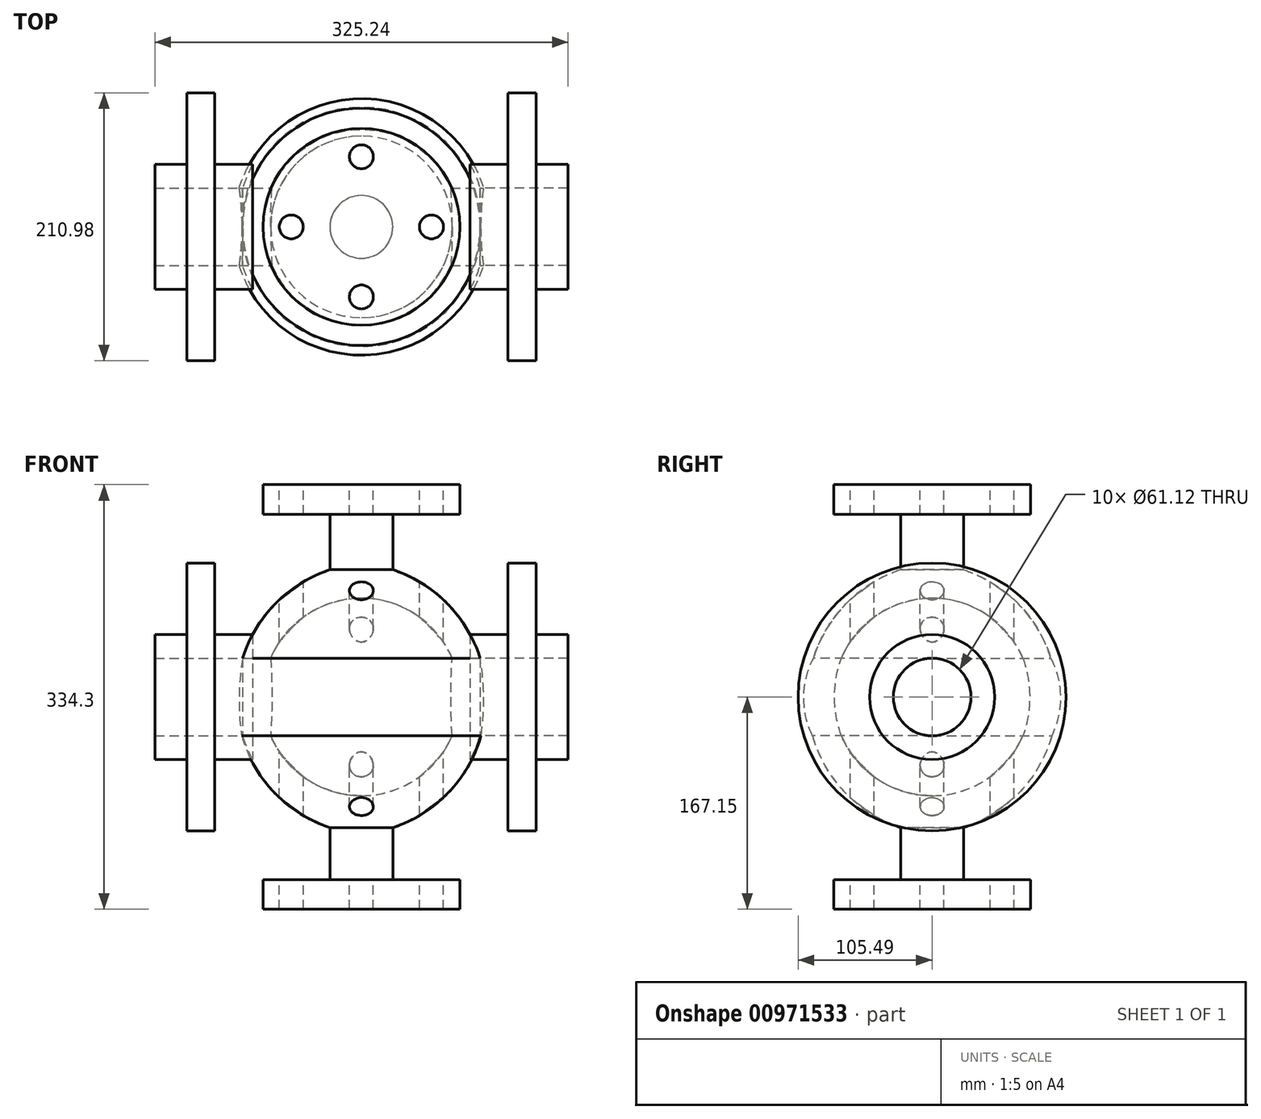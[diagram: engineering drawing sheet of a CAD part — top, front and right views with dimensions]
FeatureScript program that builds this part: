
annotation { "Feature Type Name" : "Feature", "Feature Type Description" : "" }
export const myFeature = defineFeature(function(context is Context, id is Id, definition is map)
    precondition{}
    {
        {
            var Q0;
            Q0=qCreatedBy(makeId("Front.planeOp"),FACE);
            var sketch = newSketch(context, id + "F0", { "sketchPlane" : qUnion([Q0])});
            skLineSegment(sketch, "E0", {"start": v(0, 77.72) * mm, "end": v(0, -77.72) * mm, "construction": true});
            skArc(sketch, "E1", {"start": v(0, -77.72) * mm, "mid": v(42.8, -64.87) * mm, "end": v(71.46, -30.56) * mm});
            skArc(sketch, "E2", {"start": v(23.44, -103.24) * mm, "mid": v(68, -75.84) * mm, "end": v(94.21, -30.56) * mm});
            skLineSegment(sketch, "E3", {"start": v(0, 77.72) * mm, "end": v(0, 167.15) * mm});
            skLineSegment(sketch, "E4", {"start": v(0, 167.15) * mm, "end": v(77.5, 167.15) * mm});
            skLineSegment(sketch, "E5", {"start": v(77.5, 167.15) * mm, "end": v(77.5, 143.7) * mm});
            skLineSegment(sketch, "E6", {"start": v(77.5, 143.7) * mm, "end": v(24.72, 143.7) * mm});
            skLineSegment(sketch, "E7", {"start": v(24.72, 143.7) * mm, "end": v(24.72, 100.18) * mm});
            skLineSegment(sketch, "E8", {"start": v(93.42, 30.56) * mm, "end": v(162.62, 30.56) * mm});
            skLineSegment(sketch, "E9", {"start": v(162.62, 30.56) * mm, "end": v(162.62, 49.22) * mm});
            skLineSegment(sketch, "E10", {"start": v(162.62, 49.22) * mm, "end": v(85.57, 49.22) * mm});
            skLineSegment(sketch, "E11", {"start": v(85.57, 49.22) * mm, "end": v(137.5, 49.22) * mm});
            skLineSegment(sketch, "E12", {"start": v(137.5, 49.22) * mm, "end": v(137.5, 105.49) * mm});
            skLineSegment(sketch, "E13", {"start": v(137.5, 105.49) * mm, "end": v(115.36, 105.49) * mm});
            skLineSegment(sketch, "E14", {"start": v(115.36, 105.49) * mm, "end": v(115.36, 49.22) * mm});
            skLineSegment(sketch, "E15", {"start": v(0, 0) * mm, "end": v(201.59, 0) * mm, "construction": true});
            skLineSegment(sketch, "E16.MirrorCS", {"start": v(94.21, -30.56) * mm, "end": v(162.62, -30.56) * mm});
            skLineSegment(sketch, "E17.MirrorCS", {"start": v(162.62, -30.56) * mm, "end": v(162.62, -49.22) * mm});
            skLineSegment(sketch, "E18.MirrorCS", {"start": v(162.62, -49.22) * mm, "end": v(85.57, -49.22) * mm});
            skLineSegment(sketch, "E19.MirrorCS", {"start": v(137.5, -49.22) * mm, "end": v(137.5, -105.49) * mm});
            skLineSegment(sketch, "E20.MirrorCS", {"start": v(115.36, -105.49) * mm, "end": v(115.36, -49.22) * mm});
            skLineSegment(sketch, "E21.MirrorCS", {"start": v(137.5, -105.49) * mm, "end": v(115.36, -105.49) * mm});
            skLineSegment(sketch, "E22.MirrorCS", {"start": v(24.72, -143.7) * mm, "end": v(24.72, -100.18) * mm});
            skLineSegment(sketch, "E23.MirrorCS", {"start": v(77.5, -143.7) * mm, "end": v(24.72, -143.7) * mm});
            skLineSegment(sketch, "E24.MirrorCS", {"start": v(77.5, -167.15) * mm, "end": v(77.5, -143.7) * mm});
            skLineSegment(sketch, "E25.MirrorCS", {"start": v(0, -167.15) * mm, "end": v(77.5, -167.15) * mm});
            skLineSegment(sketch, "E26.MirrorCS", {"start": v(0, -77.72) * mm, "end": v(0, -167.15) * mm});
            skPoint(sketch, "E27.orphan", {"position": v(71.46, -30.56) * mm});
            skPoint(sketch, "E28.orphan", {"position": v(71.46, 30.56) * mm});
            skArc(sketch, "E29.trimOffspring", {"start": v(93.42, 30.56) * mm, "mid": v(67.5, 73.7) * mm, "end": v(24.72, 100.18) * mm});
            skArc(sketch, "E30.trimOffspring", {"start": v(71.46, 30.56) * mm, "mid": v(42.8, 64.87) * mm, "end": v(0, 77.72) * mm});
            skArc(sketch, "E31", {"start": v(71.46, -30.56) * mm, "mid": v(76.77, 0) * mm, "end": v(71.46, 30.56) * mm});
            skArc(sketch, "E32", {"start": v(94.21, -30.56) * mm, "mid": v(100.97, 0.1) * mm, "end": v(93.42, 30.56) * mm});
            skSolve(sketch);
        }
        {
            var Q0;
            Q0=makeQuery(id+"F0.imprint","IMPRINT",FACE,{"disambiguationData":[TD([[makeQuery(id+"F0.imprint","IMPRINT",EDGE,{"derivedFrom":sQuery(id+"F0.wireOp",EDGE,"E1")}),-1.0]])]});
            var Q1;
            Q1=sQuery(id+"F0.wireOp",EDGE,"E0");
            revolve(context, id + "F1", {"surfaceOperationType" : NewSurfaceOperationType.NEW, "entities" : qUnion([Q0]), "axis" : qUnion([Q1]), "revolveType" : RevolveType.FULL});
        }
        {
            var Q0;
            {var subQ5=sQuery(id+"F0.wireOp",EDGE,"E8");Q0=makeQuery(id+"F0.imprint","IMPRINT",FACE,{"disambiguationData":[TD([[makeQuery(id+"F0.imprint","IMPRINT",EDGE,{"derivedFrom":subQ5}),1.0]])]});}
            var Q1;
            {var subQ0=sQuery(id+"F0.wireOp",EDGE,"E12");Q1=makeQuery(id+"F0.imprint","IMPRINT",FACE,{"disambiguationData":[TD([[makeQuery(id+"F0.imprint","IMPRINT",EDGE,{"derivedFrom":subQ0}),1.0]])]});}
            var Q2;
            Q2=sQuery(id+"F0.wireOp",EDGE,"E15");
            revolve(context, id + "F2", {"surfaceOperationType" : NewSurfaceOperationType.NEW, "entities" : qUnion([Q0, Q1]), "axis" : qUnion([Q2]), "revolveType" : RevolveType.FULL});
        }
        {
            var Q0;
            Q0=makeQuery(id+"F2.opRevolve","SWEPT_BODY",BODY,{"disambiguationData":[OSD([sQuery(id+"F0.wireOp",EDGE,"E8"),sQuery(id+"F0.wireOp",EDGE,"E9"),sQuery(id+"F0.wireOp",EDGE,"E10"),sQuery(id+"F0.wireOp",EDGE,"E11"),sQuery(id+"F0.wireOp",EDGE,"E12"),sQuery(id+"F0.wireOp",EDGE,"E13"),sQuery(id+"F0.wireOp",EDGE,"E14"),sQuery(id+"F0.wireOp",EDGE,"E29.trimOffspring")])]});
            var Q1;
            Q1=qCreatedBy(makeId("Right.planeOp"),FACE);
            mirror(context, id + "F3", {"entities" : qUnion([Q0]), "mirrorPlane" : qUnion([Q1])});
        }
        {
            var Q0;
            Q0=makeQuery(id+"F1.opRevolve","SWEPT_FACE",FACE,{"disambiguationData":[OSD([sQuery(id+"F0.wireOp",EDGE,"E4")])]});
            var sketch = newSketch(context, id + "F4", { "sketchPlane" : qUnion([Q0])});
            skCircle(sketch, "E33", {"center": v(0, 0) * mm, "radius": 19.05 * mm});
            skCircle(sketch, "E34", {"center": v(0, 55.18) * mm, "radius": 9.4 * mm});
            skSolve(sketch);
        }
        {
            var Q0;
            Q0=makeQuery(id+"F4.imprint","IMPRINT",FACE,{"disambiguationData":[TD([[makeQuery(id+"F4.imprint","IMPRINT",EDGE,{"derivedFrom":sQuery(id+"F4.wireOp",EDGE,"E33")}),-1.0]])]});
            var Q1;
            Q1=makeQuery(id+"F4.imprint","IMPRINT",FACE,{"disambiguationData":[TD([[makeQuery(id+"F4.imprint","IMPRINT",EDGE,{"derivedFrom":sQuery(id+"F4.wireOp",EDGE,"E34")}),1.0]])]});
            extrude(context, id + "F5", {"entities" : qUnion([Q0, Q1]), "operationType" : NewBodyOperationType.REMOVE, "endBound" : BoundingType.THROUGH_ALL, "oppositeDirection" : true, "depth" : 25.4 * mm, "offsetDistance" : 25.4 * mm});
        }
        {
            var Q0;
            Q0=makeQuery(id+"F1.opRevolve","SWEPT_BODY",BODY,{"disambiguationData":[OSD([sQuery(id+"F0.wireOp",EDGE,"E1"),sQuery(id+"F0.wireOp",EDGE,"E2"),sQuery(id+"F0.wireOp",EDGE,"E3"),sQuery(id+"F0.wireOp",EDGE,"E4"),sQuery(id+"F0.wireOp",EDGE,"E5"),sQuery(id+"F0.wireOp",EDGE,"E6"),sQuery(id+"F0.wireOp",EDGE,"E7"),sQuery(id+"F0.wireOp",EDGE,"E22.MirrorCS"),sQuery(id+"F0.wireOp",EDGE,"E23.MirrorCS"),sQuery(id+"F0.wireOp",EDGE,"E24.MirrorCS"),sQuery(id+"F0.wireOp",EDGE,"E25.MirrorCS"),sQuery(id+"F0.wireOp",EDGE,"E26.MirrorCS"),sQuery(id+"F0.wireOp",EDGE,"E29.trimOffspring"),sQuery(id+"F0.wireOp",EDGE,"E30.trimOffspring"),sQuery(id+"F0.wireOp",EDGE,"E31"),sQuery(id+"F0.wireOp",EDGE,"E32")])]});
            var Q1;
            Q1=sQuery(id+"F0.wireOp",EDGE,"E0");
            circularPattern(context, id + "F6", {"entities" : qUnion([Q0]), "axis" : qUnion([Q1]), "angle" : 360 * degree, "instanceCount" : 4, "equalSpace" : true});
        }
        {
            var Q0;
            Q0=makeQuery(id+"F2.opRevolve","SWEPT_FACE",FACE,{"disambiguationData":[OSD([sQuery(id+"F0.wireOp",EDGE,"E9")])]});
            var sketch = newSketch(context, id + "F7", { "sketchPlane" : qUnion([Q0])});
            skCircle(sketch, "E35.0", {"center": v(0, 0) * mm, "radius": 30.56 * mm});
            skSolve(sketch);
        }
        {
            var Q0;
            Q0=qSketchRegion(id+"F7",true);
            extrude(context, id + "F8", {"entities" : qUnion([Q0]), "operationType" : NewBodyOperationType.REMOVE, "endBound" : BoundingType.THROUGH_ALL, "oppositeDirection" : true, "depth" : 25.4 * mm, "offsetDistance" : 25.4 * mm});
        }
    });
